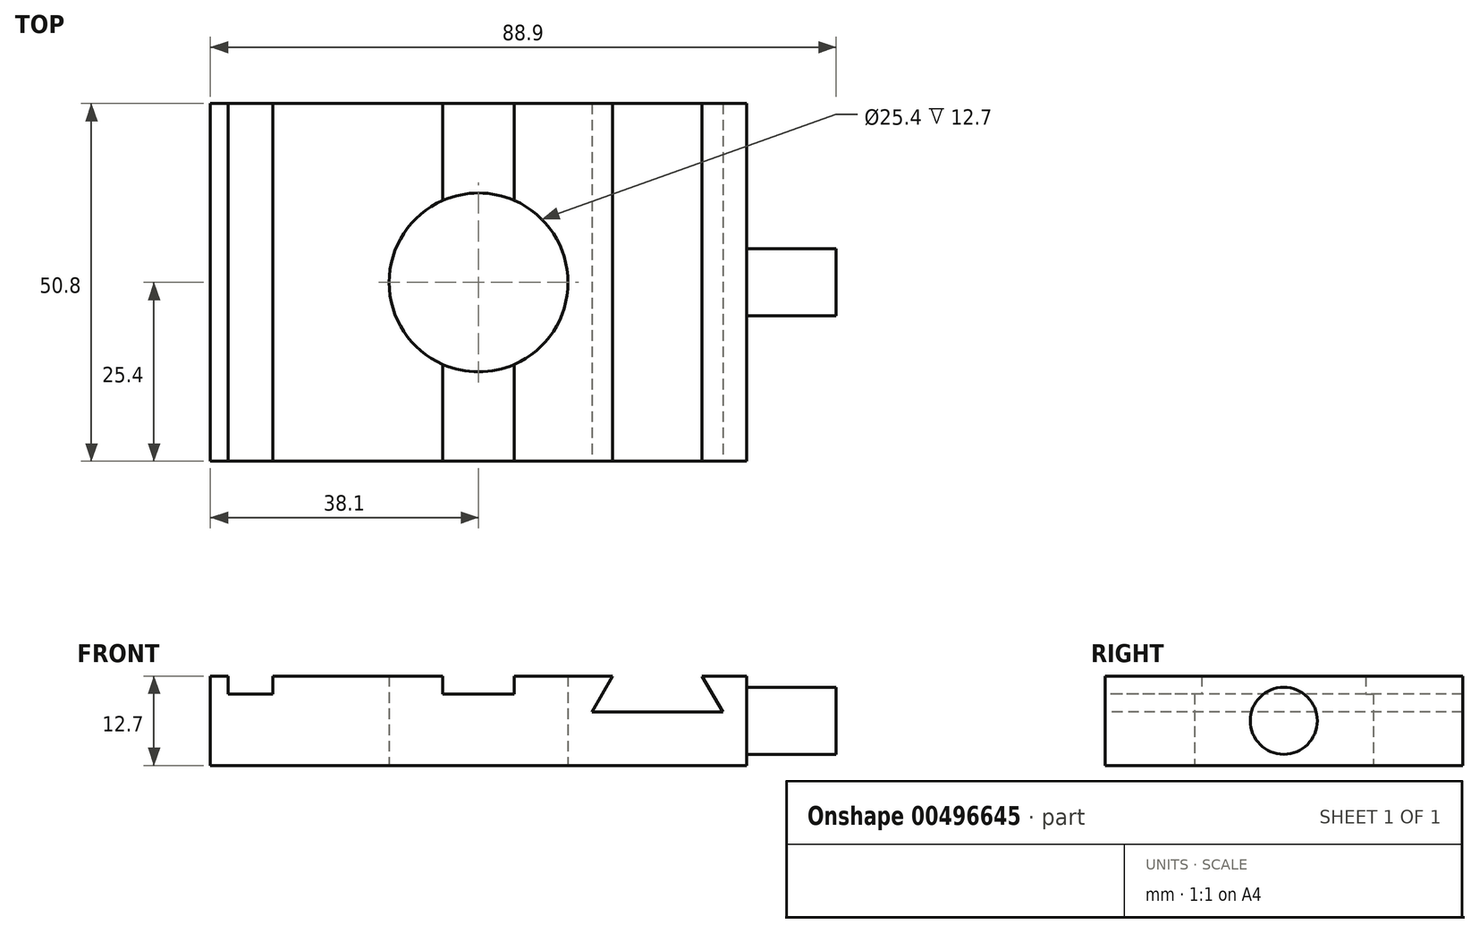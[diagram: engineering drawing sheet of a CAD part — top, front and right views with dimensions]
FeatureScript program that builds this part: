
annotation { "Feature Type Name" : "Feature", "Feature Type Description" : "" }
export const myFeature = defineFeature(function(context is Context, id is Id, definition is map)
    precondition{}
    {
        {
            var Q0;
            Q0=qCreatedBy(makeId("Top.planeOp"),FACE);
            var sketch = newSketch(context, id + "F0", { "sketchPlane" : qUnion([Q0])});
            skLineSegment(sketch, "E0.bottom", {"start": v(38.1, 25.4) * mm, "end": v(-38.1, 25.4) * mm});
            skLineSegment(sketch, "E0.top", {"start": v(38.1, -25.4) * mm, "end": v(-38.1, -25.4) * mm});
            skLineSegment(sketch, "E0.left", {"start": v(38.1, 25.4) * mm, "end": v(38.1, -25.4) * mm});
            skLineSegment(sketch, "E0.right", {"start": v(-38.1, 25.4) * mm, "end": v(-38.1, -25.4) * mm});
            skPoint(sketch, "E0.middle", {"position": v(0, 0) * mm});
            skCircle(sketch, "E1", {"center": v(0, 0) * mm, "radius": 12.7 * mm});
            skSolve(sketch);
        }
        {
            var Q0;
            Q0 = qSketchRegion(id + "F0", true);
            extrude(context, id + "F1", {"entities" : qUnion([Q0]), "depth" : 12.7 * mm, "offsetDistance" : 25 * mm});
        }
        {
            var Q0;
            Q0=makeQuery(id+"F1.opExtrude","CAP_FACE",FACE,{"disambiguationData":[OSD([sQuery(id+"F0.wireOp",EDGE,"E0.bottom"),sQuery(id+"F0.wireOp",EDGE,"E0.top"),sQuery(id+"F0.wireOp",EDGE,"E0.left"),sQuery(id+"F0.wireOp",EDGE,"E0.right"),sQuery(id+"F0.wireOp",EDGE,"E1")])],"isStart":false});
            var sketch = newSketch(context, id + "F2", { "sketchPlane" : qUnion([Q0])});
            skLineSegment(sketch, "E2.bottom", {"start": v(-35.56, 25.4) * mm, "end": v(-29.21, 25.4) * mm});
            skLineSegment(sketch, "E2.top", {"start": v(-35.56, -25.4) * mm, "end": v(-29.21, -25.4) * mm});
            skLineSegment(sketch, "E2.left", {"start": v(-35.56, 25.4) * mm, "end": v(-35.56, -25.4) * mm});
            skLineSegment(sketch, "E2.right", {"start": v(-29.21, 25.4) * mm, "end": v(-29.21, -25.4) * mm});
            skLineSegment(sketch, "E3.bottom", {"start": v(-5.08, 25.4) * mm, "end": v(5.08, 25.4) * mm});
            skLineSegment(sketch, "E3.top", {"start": v(-5.08, -25.4) * mm, "end": v(5.08, -25.4) * mm});
            skLineSegment(sketch, "E3.left", {"start": v(-5.08, 25.4) * mm, "end": v(-5.08, -25.4) * mm});
            skLineSegment(sketch, "E3.right", {"start": v(5.08, 25.4) * mm, "end": v(5.08, -25.4) * mm});
            skPoint(sketch, "E4", {"position": v(0, 0) * mm});
            skLineSegment(sketch, "E5", {"start": v(0, 25.4) * mm, "end": v(0, -25.4) * mm, "construction": true});
            skSolve(sketch);
        }
        {
            var Q0;
            Q0 = qSketchRegion(id + "F2", true);
            extrude(context, id + "F3", {"entities" : qUnion([Q0]), "operationType" : NewBodyOperationType.REMOVE, "oppositeDirection" : true, "depth" : 2.54 * mm, "offsetDistance" : 25 * mm});
        }
        {
            var Q0;
            Q0=makeQuery(id+"F1.opExtrude","SWEPT_FACE",FACE,{"disambiguationData":[OSD([sQuery(id+"F0.wireOp",EDGE,"E0.top")])]});
            var sketch = newSketch(context, id + "F4", { "sketchPlane" : qUnion([Q0])});
            skLineSegment(sketch, "E6", {"start": v(19.05, 12.7) * mm, "end": v(16.12, 7.62) * mm});
            skLineSegment(sketch, "E7", {"start": v(16.12, 7.62) * mm, "end": v(34.68, 7.62) * mm});
            skLineSegment(sketch, "E8", {"start": v(34.68, 7.62) * mm, "end": v(31.75, 12.7) * mm});
            skLineSegment(sketch, "E9", {"start": v(19.05, 12.7) * mm, "end": v(31.75, 12.7) * mm});
            skLineSegment(sketch, "E10", {"start": v(25.4, 7.62) * mm, "end": v(25.4, 12.7) * mm, "construction": true});
            skSolve(sketch);
        }
        {
            var Q0;
            Q0 = qSketchRegion(id + "F4", true);
            extrude(context, id + "F5", {"entities" : qUnion([Q0]), "operationType" : NewBodyOperationType.REMOVE, "endBound" : BoundingType.UP_TO_NEXT, "oppositeDirection" : true, "depth" : 25 * mm, "offsetDistance" : 25 * mm});
        }
        {
            var Q0;
            Q0=makeQuery(id+"F1.opExtrude","SWEPT_FACE",FACE,{"disambiguationData":[OSD([sQuery(id+"F0.wireOp",EDGE,"E0.left")])]});
            var sketch = newSketch(context, id + "F6", { "sketchPlane" : qUnion([Q0])});
            skCircle(sketch, "E11", {"center": v(0, 6.35) * mm, "radius": 4.76 * mm});
            skPoint(sketch, "E11.centerSnap0", {"position": v(0, 12.7) * mm});
            skPoint(sketch, "E11.centerSnap1", {"position": v(-25.4, 6.35) * mm});
            skSolve(sketch);
        }
        {
            var Q0;
            Q0 = qSketchRegion(id + "F6", true);
            extrude(context, id + "F7", {"entities" : qUnion([Q0]), "operationType" : NewBodyOperationType.ADD, "depth" : 12.7 * mm, "offsetDistance" : 25 * mm});
        }
    });
